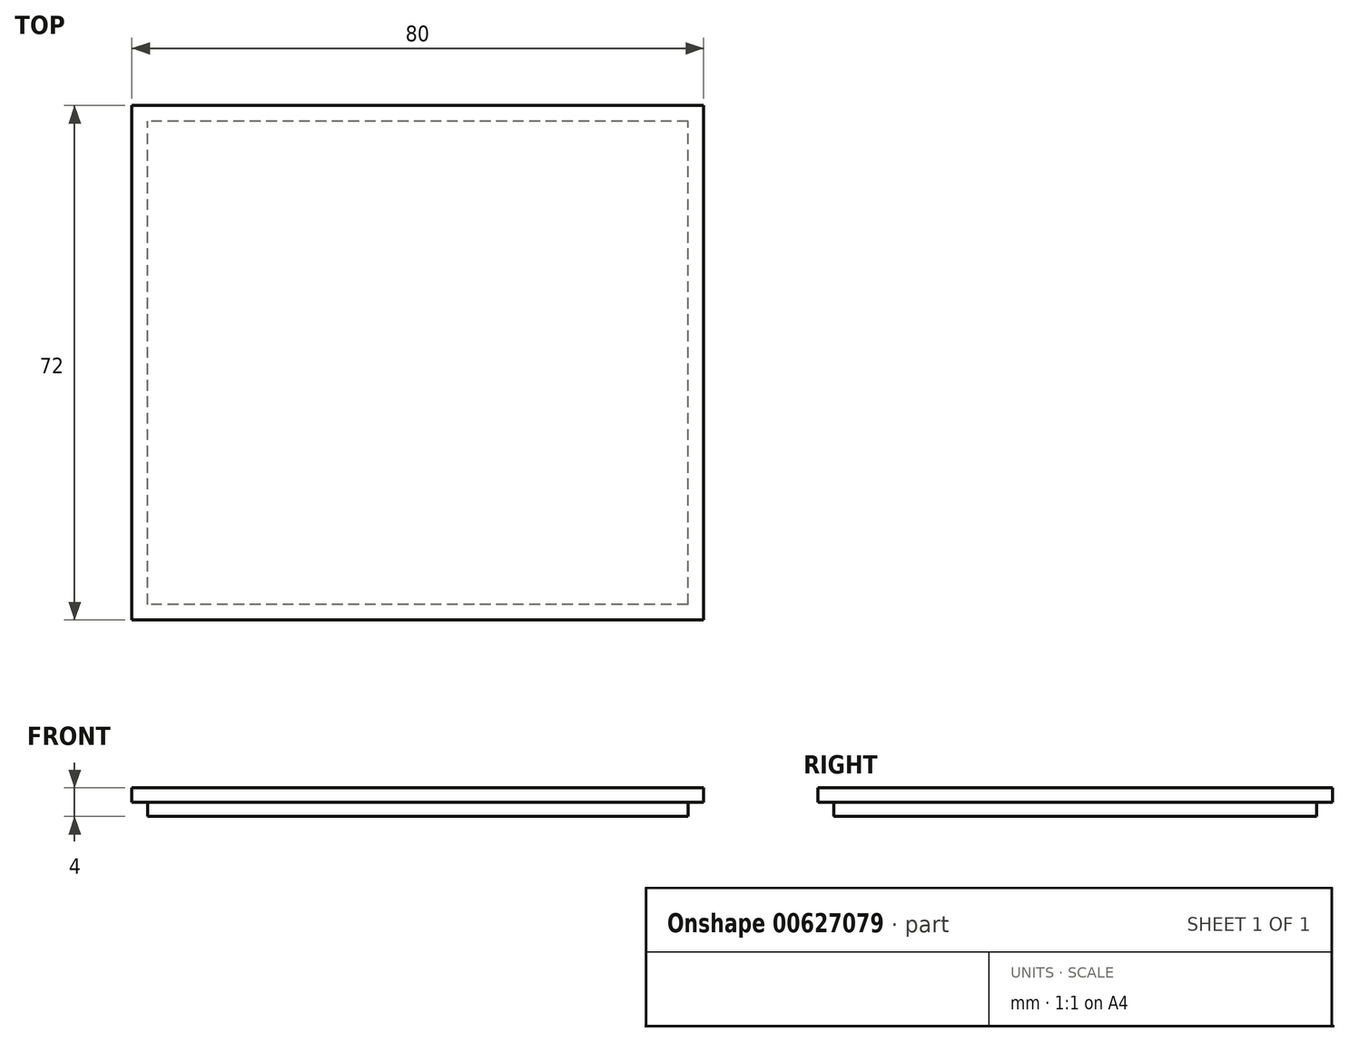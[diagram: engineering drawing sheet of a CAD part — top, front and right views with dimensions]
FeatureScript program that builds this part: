
annotation { "Feature Type Name" : "Feature", "Feature Type Description" : "" }
export const myFeature = defineFeature(function(context is Context, id is Id, definition is map)
    precondition{}
    {
        {
            var Q0;
            Q0=qCreatedBy(makeId("Top.planeOp"),FACE);
            var sketch = newSketch(context, id + "F0", { "sketchPlane" : qUnion([Q0])});
            skLineSegment(sketch, "E0.bottom", {"start": v(0, -1.18) * mm, "end": v(80, -1.18) * mm});
            skLineSegment(sketch, "E0.top", {"start": v(0, 70.82) * mm, "end": v(80, 70.82) * mm});
            skLineSegment(sketch, "E0.left", {"start": v(0, -1.18) * mm, "end": v(0, 70.82) * mm});
            skLineSegment(sketch, "E0.right", {"start": v(80, -1.18) * mm, "end": v(80, 70.82) * mm});
            skLineSegment(sketch, "E1.bottom", {"start": v(0, 70.82) * mm, "end": v(2, 70.82) * mm, "construction": true});
            skLineSegment(sketch, "E1.top", {"start": v(0, 68.82) * mm, "end": v(2, 68.82) * mm, "construction": true});
            skLineSegment(sketch, "E1.left", {"start": v(0, 70.82) * mm, "end": v(0, 68.82) * mm, "construction": true});
            skLineSegment(sketch, "E1.right", {"start": v(2, 70.82) * mm, "end": v(2, 68.82) * mm, "construction": true});
            skLineSegment(sketch, "E2.bottom", {"start": v(80, -1.18) * mm, "end": v(78, -1.18) * mm, "construction": true});
            skLineSegment(sketch, "E2.top", {"start": v(80, 0.82) * mm, "end": v(78, 0.82) * mm, "construction": true});
            skLineSegment(sketch, "E2.left", {"start": v(80, -1.18) * mm, "end": v(80, 0.82) * mm, "construction": true});
            skLineSegment(sketch, "E2.right", {"start": v(78, -1.18) * mm, "end": v(78, 0.82) * mm, "construction": true});
            skSolve(sketch);
        }
        {
            var Q0;
            Q0 = qSketchRegion(id + "F0", true);
            extrude(context, id + "F1", {"entities" : qUnion([Q0]), "depth" : 2 * mm, "offsetDistance" : 25 * mm});
        }
        {
            var Q0;
            Q0=makeQuery(id+"F1.opExtrude","CAP_FACE",FACE,{"disambiguationData":[OSD([sQuery(id+"F0.wireOp",EDGE,"E0.bottom"),sQuery(id+"F0.wireOp",EDGE,"E0.top"),sQuery(id+"F0.wireOp",EDGE,"E0.left"),sQuery(id+"F0.wireOp",EDGE,"E0.right")])],"isStart":true});
            var sketch = newSketch(context, id + "F2", { "sketchPlane" : qUnion([Q0])});
            skLineSegment(sketch, "E3.bottom", {"start": v(80, 1.18) * mm, "end": v(77.8, 1.18) * mm, "construction": true});
            skLineSegment(sketch, "E3.top", {"start": v(80, -1.02) * mm, "end": v(77.8, -1.02) * mm, "construction": true});
            skLineSegment(sketch, "E3.left", {"start": v(80, 1.18) * mm, "end": v(80, -1.02) * mm, "construction": true});
            skLineSegment(sketch, "E3.right", {"start": v(77.8, 1.18) * mm, "end": v(77.8, -1.02) * mm, "construction": true});
            skLineSegment(sketch, "E4.bottom", {"start": v(0, -70.82) * mm, "end": v(2.2, -70.82) * mm, "construction": true});
            skLineSegment(sketch, "E4.top", {"start": v(0, -68.62) * mm, "end": v(2.2, -68.62) * mm, "construction": true});
            skLineSegment(sketch, "E4.left", {"start": v(0, -70.82) * mm, "end": v(0, -68.62) * mm, "construction": true});
            skLineSegment(sketch, "E4.right", {"start": v(2.2, -70.82) * mm, "end": v(2.2, -68.62) * mm, "construction": true});
            skLineSegment(sketch, "E5.bottom", {"start": v(77.8, -1.02) * mm, "end": v(2.2, -1.02) * mm});
            skLineSegment(sketch, "E5.top", {"start": v(77.8, -68.62) * mm, "end": v(2.2, -68.62) * mm});
            skLineSegment(sketch, "E5.left", {"start": v(77.8, -1.02) * mm, "end": v(77.8, -68.62) * mm});
            skLineSegment(sketch, "E5.right", {"start": v(2.2, -1.02) * mm, "end": v(2.2, -68.62) * mm});
            skSolve(sketch);
        }
        {
            var Q0;
            Q0 = qSketchRegion(id + "F2", true);
            extrude(context, id + "F3", {"entities" : qUnion([Q0]), "operationType" : NewBodyOperationType.ADD, "depth" : 2 * mm, "offsetDistance" : 25 * mm});
        }
    });
